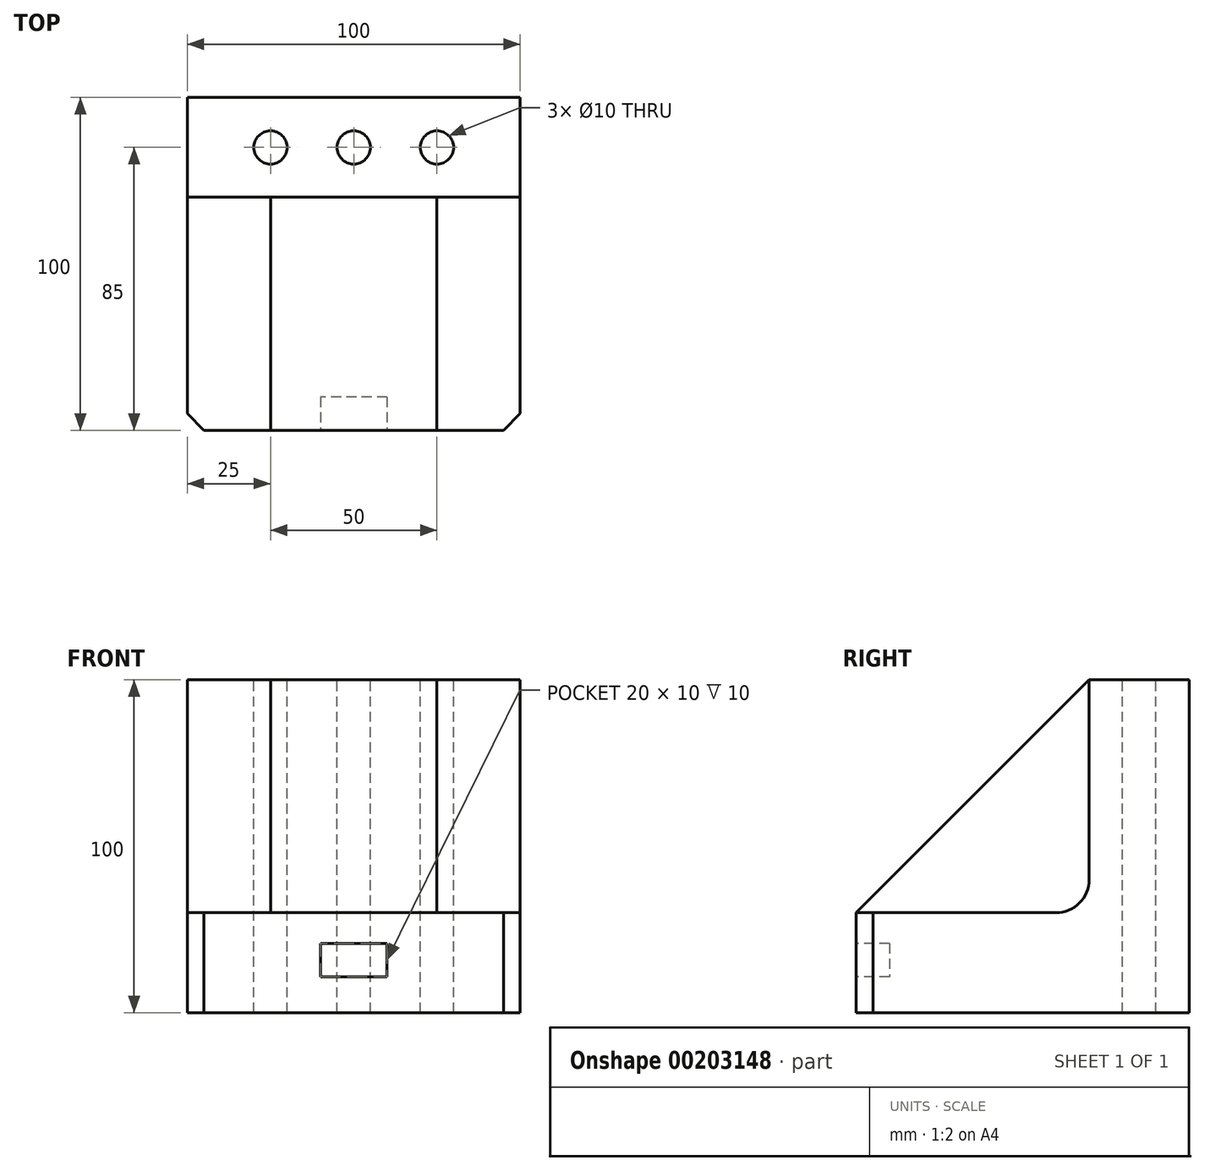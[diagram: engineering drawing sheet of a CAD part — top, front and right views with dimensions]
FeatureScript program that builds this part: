
annotation { "Feature Type Name" : "Feature", "Feature Type Description" : "" }
export const myFeature = defineFeature(function(context is Context, id is Id, definition is map)
    precondition{}
    {
        {
            var Q0;
            Q0=qCreatedBy(makeId("Right.planeOp"),FACE);
            var sketch = newSketch(context, id + "F0", { "sketchPlane" : qUnion([Q0])});
            skLineSegment(sketch, "E0", {"start": v(0, 0) * mm, "end": v(0, 100) * mm});
            skLineSegment(sketch, "E1", {"start": v(0, 100) * mm, "end": v(-30, 100) * mm});
            skLineSegment(sketch, "E2", {"start": v(-30, 100) * mm, "end": v(-100, 30) * mm});
            skLineSegment(sketch, "E3", {"start": v(-100, 30) * mm, "end": v(-100, 0) * mm});
            skLineSegment(sketch, "E4", {"start": v(-100, 0) * mm, "end": v(0, 0) * mm});
            skSolve(sketch);
        }
        {
            var Q0;
            Q0=makeQuery(id+"F0.imprint","IMPRINT",FACE,{"disambiguationData":[TD([[makeQuery(id+"F0.imprint","IMPRINT",EDGE,{"derivedFrom":sQuery(id+"F0.wireOp",EDGE,"E0")}),1.0]])]});
            extrude(context, id + "F1", {"entities" : qUnion([Q0]), "depth" : 100 * mm});
        }
        {
            var Q0;
            Q0=makeQuery(id+"F1.opExtrude","CAP_FACE",FACE,{"disambiguationData":[OSD([sQuery(id+"F0.wireOp",EDGE,"E0"),sQuery(id+"F0.wireOp",EDGE,"E1"),sQuery(id+"F0.wireOp",EDGE,"E2"),sQuery(id+"F0.wireOp",EDGE,"E3"),sQuery(id+"F0.wireOp",EDGE,"E4")])],"isStart":true});
            var sketch = newSketch(context, id + "F2", { "sketchPlane" : qUnion([Q0])});
            skLineSegment(sketch, "E5", {"start": v(30, 100) * mm, "end": v(30, 40) * mm});
            skLineSegment(sketch, "E6", {"start": v(40, 30) * mm, "end": v(100, 30) * mm});
            skPoint(sketch, "E7.visualSharp", {"position": v(30, 30) * mm});
            skArc(sketch, "E7.filletArc", {"start": v(30, 40) * mm, "mid": v(32.93, 32.93) * mm, "end": v(40, 30) * mm});
            skSolve(sketch);
        }
        {
            var Q0;
            Q0=makeQuery(id+"F2.imprint","IMPRINT",FACE,{"disambiguationData":[TD([[makeQuery(id+"F2.imprint","IMPRINT",EDGE,{"derivedFrom":sQuery(id+"F2.wireOp",EDGE,"E5")}),1.0]])]});
            extrude(context, id + "F3", {"entities" : qUnion([Q0]), "operationType" : NewBodyOperationType.REMOVE, "oppositeDirection" : true, "depth" : 25 * mm});
        }
        {
            var Q0;
            Q0=makeQuery(id+"F1.opExtrude","CAP_FACE",FACE,{"disambiguationData":[OSD([sQuery(id+"F0.wireOp",EDGE,"E0"),sQuery(id+"F0.wireOp",EDGE,"E1"),sQuery(id+"F0.wireOp",EDGE,"E2"),sQuery(id+"F0.wireOp",EDGE,"E3"),sQuery(id+"F0.wireOp",EDGE,"E4")])],"isStart":false});
            var sketch = newSketch(context, id + "F4", { "sketchPlane" : qUnion([Q0])});
            skLineSegment(sketch, "E8", {"start": v(-30, 100) * mm, "end": v(-30, 40) * mm});
            skLineSegment(sketch, "E9", {"start": v(-40, 30) * mm, "end": v(-100, 30) * mm});
            skPoint(sketch, "E10.visualSharp", {"position": v(-30, 30) * mm});
            skArc(sketch, "E10.filletArc", {"start": v(-40, 30) * mm, "mid": v(-32.93, 32.93) * mm, "end": v(-30, 40) * mm});
            skSolve(sketch);
        }
        {
            var Q0;
            Q0=makeQuery(id+"F4.imprint","IMPRINT",FACE,{"disambiguationData":[TD([[makeQuery(id+"F4.imprint","IMPRINT",EDGE,{"derivedFrom":sQuery(id+"F4.wireOp",EDGE,"E8")}),-1.0]])]});
            extrude(context, id + "F5", {"entities" : qUnion([Q0]), "operationType" : NewBodyOperationType.REMOVE, "oppositeDirection" : true, "depth" : 25 * mm});
        }
        {
            var Q0;
            Q0=makeQuery(id+"F1.opExtrude","SWEPT_FACE",FACE,{"disambiguationData":[OSD([sQuery(id+"F0.wireOp",EDGE,"E1")])]});
            var sketch = newSketch(context, id + "F6", { "sketchPlane" : qUnion([Q0])});
            skCircle(sketch, "E11", {"center": v(25, -15) * mm, "radius": 5 * mm});
            skCircle(sketch, "E12", {"center": v(50, -15) * mm, "radius": 5 * mm});
            skCircle(sketch, "E13", {"center": v(75, -15) * mm, "radius": 5 * mm});
            skSolve(sketch);
        }
        {
            var Q0;
            Q0 = qSketchRegion(id + "F6", true);
            extrude(context, id + "F7", {"entities" : qUnion([Q0]), "operationType" : NewBodyOperationType.REMOVE, "oppositeDirection" : true, "depth" : 100 * mm});
        }
        {
            var Q0;
            Q0=makeQuery(id+"F1.opExtrude","SWEPT_FACE",FACE,{"disambiguationData":[OSD([sQuery(id+"F0.wireOp",EDGE,"E3")])]});
            var sketch = newSketch(context, id + "F8", { "sketchPlane" : qUnion([Q0])});
            skLineSegment(sketch, "E14", {"start": v(40, 20.75) * mm, "end": v(40, 10.75) * mm});
            skLineSegment(sketch, "E15", {"start": v(40, 10.75) * mm, "end": v(60, 10.75) * mm});
            skLineSegment(sketch, "E16", {"start": v(60, 10.75) * mm, "end": v(60, 20.75) * mm});
            skLineSegment(sketch, "E17", {"start": v(60, 20.75) * mm, "end": v(40, 20.75) * mm});
            skSolve(sketch);
        }
        {
            var Q0;
            Q0=makeQuery(id+"F8.imprint","IMPRINT",FACE,{"disambiguationData":[TD([[makeQuery(id+"F8.imprint","IMPRINT",EDGE,{"derivedFrom":sQuery(id+"F8.wireOp",EDGE,"E14")}),1.0]])]});
            var Q1;
            Q1 = qSketchRegion(id + "F8", true);
            extrude(context, id + "F9", {"entities" : qUnion([Q0, Q1]), "operationType" : NewBodyOperationType.REMOVE, "oppositeDirection" : true, "depth" : 10 * mm});
        }
        {
            var Q0;
            Q0=makeQuery(id+"F1.opExtrude","CAP_EDGE",EDGE,{"disambiguationData":[OSD([sQuery(id+"F0.wireOp",EDGE,"E3")])],"isStart":true});
            chamfer(context, id + "F10", {"entities" : qUnion([Q0]), "width" : 5 * mm, "tangentPropagation" : true});
        }
        {
            var Q0;
            Q0=makeQuery(id+"F1.opExtrude","CAP_EDGE",EDGE,{"disambiguationData":[OSD([sQuery(id+"F0.wireOp",EDGE,"E3")])],"isStart":false});
            chamfer(context, id + "F11", {"entities" : qUnion([Q0]), "width" : 5 * mm, "tangentPropagation" : true});
        }
    });
